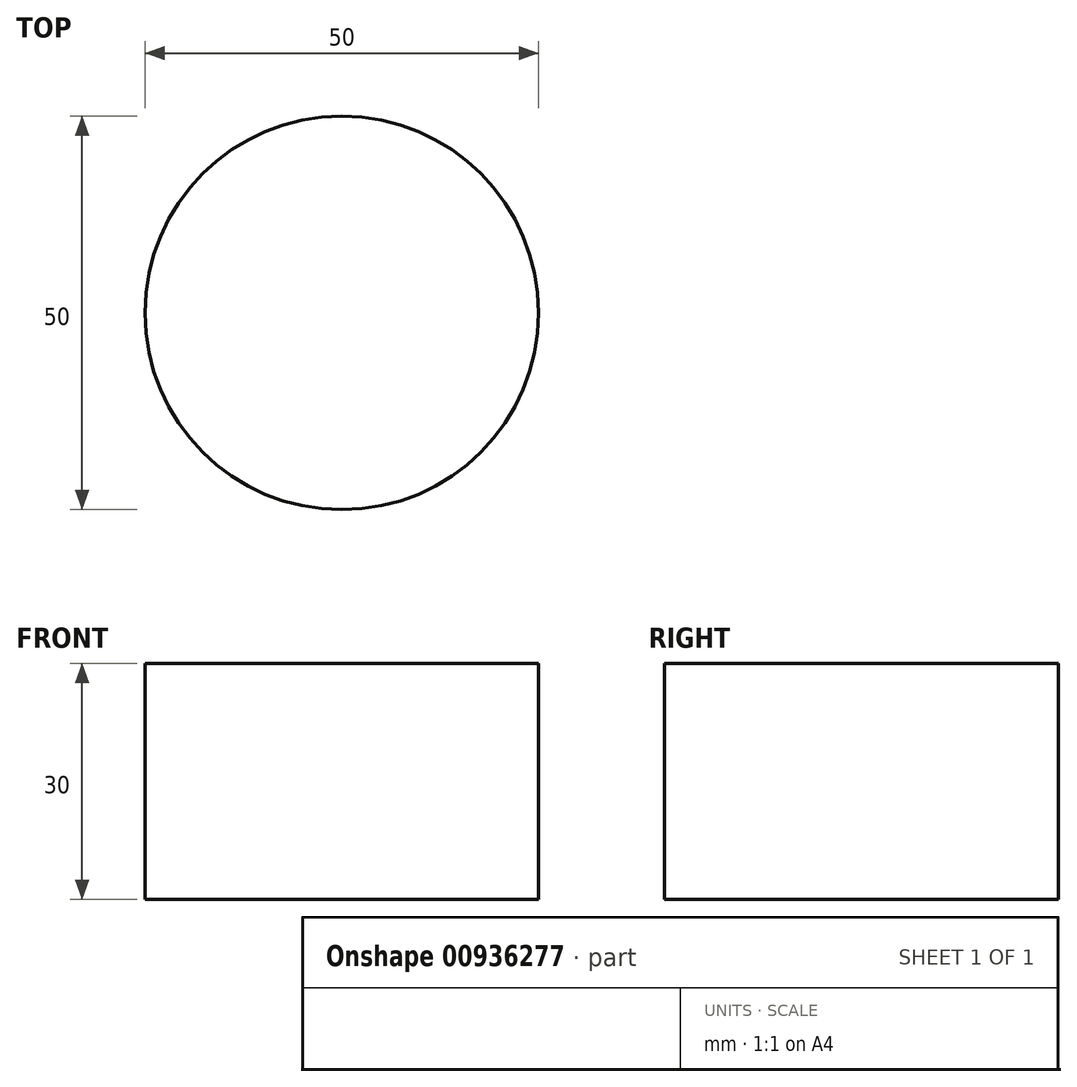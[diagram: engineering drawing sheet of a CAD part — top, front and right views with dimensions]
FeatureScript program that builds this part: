
annotation { "Feature Type Name" : "Feature", "Feature Type Description" : "" }
export const myFeature = defineFeature(function(context is Context, id is Id, definition is map)
    precondition{}
    {
        {
            var Q0;
            Q0=qCreatedBy(makeId("Top.planeOp"),FACE);
            var sketch = newSketch(context, id + "F0", { "sketchPlane" : qUnion([Q0])});
            skCircle(sketch, "E0", {"center": v(0, 0) * mm, "radius": 25 * mm});
            skSolve(sketch);
        }
        {
            var Q0;
            Q0 = qSketchRegion(id + "F0", true);
            extrude(context, id + "F1", {"entities" : qUnion([Q0]), "depth" : 30 * mm, "offsetDistance" : 25 * mm});
        }
    });
